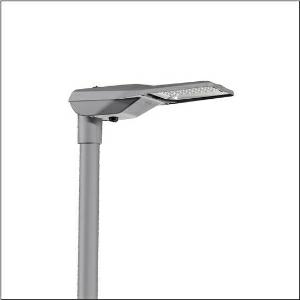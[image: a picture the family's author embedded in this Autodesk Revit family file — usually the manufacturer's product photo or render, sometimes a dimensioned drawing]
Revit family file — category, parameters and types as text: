
# Revit family: streetlight_sl_21_mini___p1_0a_5xe2a33t08hb_97bb
name_source: partatom
category: Lighting Fixtures
units: mm (PartAtom-declared; Revit-internal decimal feet)

## family parameters
Cut with Voids When Loaded = No
Host = Face
Light Source = No
Part Type = Normal
Room Calculation Point = No
Round Connector Dimension = Use Diameter
Shared = No

## types (1)
- --- (1 x LED, 9040 lm, 66 W, 3000K)
    Apparent Load = 66 VA
    CIE Flux Codes = 21 50 90 100 100
    Color Rendering = 70
    Color Temperature = 3000K
    Default Elevation = 1800 mm
    Description = Streetlight SL 21 mini, mast luminaire, primary light control with lens, of PMMA, primary optical cover: cover, of toughened safety glass, transparent, light distribution: P1.0a, light emission: direct distribution, primary light characteristic: asymmetric, installation type: side-entry, post-top, LED, High Power LED, rated luminous flux: 9.040lm, luminous efficacy: 137lm/W, light colour: 730, colour temperature: 3000K, control gear: D4i, control: overheat protection, constant luminous flux control, time-dependent luminous flux control, flexible luminous flux parameterisation, pre-setting: logarithmic dimming characteristic, mains connection: 220..240V, AC, 50/60Hz, start of lifetime: 66W, end of service life: 69W, reduction: 30W, luminaire housing, of diecast aluminium, powder-coated, SITECO metallic grey (DB 702S), corrosivity category C5 high according to DIN EN ISO 12944, please order mast flange separately, inclination adjustable: 0°, 5°, 10°, 15°, sealing non-destructively replaceable, multi-level sealing system, length: 628mm, width: 235mm, height: 110mm, mast flange for spigot size: 42mm (side-entry): 5XC10008XM4, 60/48mm (side-entry/post-top): 5XC10108XM2, 76/60mm (side-entry/post-top): 5XC10108XM1, mounting height: 4..8m, Smart Interface below and above, protection rating (complete): IP66, insulation class (complete): insulation class II (safety insulation), certification: CE, ENEC, ENEC+, VDE, impact resistance: IK10, permissible operating ambient temperature for outdoor applications: -40..+50°C, standard-compliant lighting for roads and squares, packaging unit: 1 piece

Light Distribution: P1.0a
    Height = 110 mm
    Lamp = 1 x LED
    Lamp Light Flux = 9040 lm
    Lamp Power = 66 W
    Lamp count = 1
    Length = 625 mm
    Luminous efficacy = 137 lm/W
    Manufacturer = Siteco
    ModVariant = No
    Model = 5XE2A33T08HB
    Number of Poles = 1
    OnlyDefault = Yes
    Power Factor = 1
    Product Name = Streetlight SL 21 mini | P1.0a
    Product group = mast luminaire | pylon top
    ProductGroupID = 6100
    Protection Class = Protection class II
    Protection Degree = IP 66
    RLX_Detail_Level = 1
    RLX_Emergency_Light_Flux = 0 lm
    RLX_Emergency_Type = 0
    RLX_Emergency_Type_DB = No
    RlxData = <blob elided: 37561 chars, md5=08d0e1f6>
    Socket = socket
    Standby Power = 0 W
    System Light Flux = 9040 lm
    System Power = 66 W
    Type Comments = factory setting: luminous flux: 100 % | dim-lin: 254 | 670 mA
    Type Image = l_1003514.jpg
    URL = http://relux.com
    VarID = @adj_183943
    Voltage = 0 V
    Weight = 0.00 kg
    Width = 234 mm

## geometry (parser evidence)
native form markers: Blend x4, Sweep x12
no freeform markers — native parametric forms only
